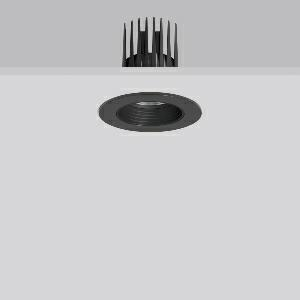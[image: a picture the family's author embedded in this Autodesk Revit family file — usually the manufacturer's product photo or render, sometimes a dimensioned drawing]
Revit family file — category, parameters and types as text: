
# Revit family: heledon_mini_e_901743_003_1_b71d
name_source: partatom
category: Lighting Fixtures
units: mm (PartAtom-declared; Revit-internal decimal feet)

## family parameters
Cut with Voids When Loaded = No
Host = Face
Light Source = No
Part Type = Normal
Room Calculation Point = No
Round Connector Dimension = Use Diameter
Shared = No

## types (1)
- HELEDON mini E (1 x LED Modul 940, 2400 lm, 4000)
    Apparent Load = 20 VA
    Approval mark = CE
    CIE Flux Codes = 99 100 100 100 100
    Color Rendering = 92
    Color Temperature = 4000
    Default Elevation = 1800 mm
    Description = Series: HELEDON mini
Round recessed downlight. Housing: die-cast aluminium, powder-coated. Black plastic ring and recessed LED to prevent glare from the side. Optical assembly with lens made of plastic (polycarbonate) for the best homogeneous light distribution - can be changed without tools. Best colour rendering index Ra>90. Suitable for Recessed ceiling mounting. Installation without tools thanks to spring fastening system. Including separate LED converter with connecting cable 600 mm.High quality converter without flickering and stroboscopic effect. Through-wiring box (5 pole) available as accessory. The following accessories can be mounted without use of tools: interchangeable lenses, decorative glasses, honeycomb louvre, clear and frosted diffusers, white interchangeable plastic ring. 
Colour: deep black, matt (RAL 9005)
Diameter: 124 mm
Height: 3 mm
Cut-out diameter: 114 mm
Recess height: 170 mm
Luminaire: recess height: 120 mm
Lamp: LED
Socket: without socket
Colour temperature: 4000K
Colour rendering index (CRI): 92
System power: 20 W
Rated luminous flux: 2400 lm
Luminous efficiency: 120 lm/W
Control gear: Regulated power supply
Protection class: II
Type of protection: IP 20
    Height = 0 mm  [stored 0 ft]
    Lamp = 1 x LED Modul 940
    Lamp Light Flux = 2400 lm
    Lamp count = 1
    Length = 124 mm  [stored 0.406824 ft]
    Lifetime = 50000 h
    Luminous efficacy = 120 lm/W
    Manufacturer = RZB
    ModVariant = No
    Model = 901743.003.1
    Mounting Place = Ceiling
    Mounting Type = Recessed
    Number of Poles = 1
    OnlyDefault = Yes
    Power Factor = 1
    Product Name = HELEDON mini E
    Product group = Recessed downlights
    ProductGroupID = 402
    Protection Class = Protection class II
    Protection Degree = IP 20
    RLX_Detail_Level = 1
    RLX_Emergency_Light_Flux = 0 lm
    RLX_Emergency_Type = 0
    RLX_Emergency_Type_DB = No
    RlxData = <blob elided: 125097 chars, md5=2e85dcb2>
    Socket = socket
    Standby Power = 0 W
    System Light Flux = 2400 lm
    System Power = 20 W
    Type Comments = Product without accessories
    Type Image = 901656.003.jpg
    URL = http://relux.com
    VarID = ---
    Voltage = 230 V
    Voltage Range = 220-240 V
    Weight = 0.00 kg
    Width = 0 mm  [stored 0 ft]

note: [stored X ft] marks values corroborated as IEEE doubles in the binary element streams (Revit-internal decimal feet)

## geometry (parser evidence)
native form markers: Blend x4, Sweep x11
no freeform markers — native parametric forms only
